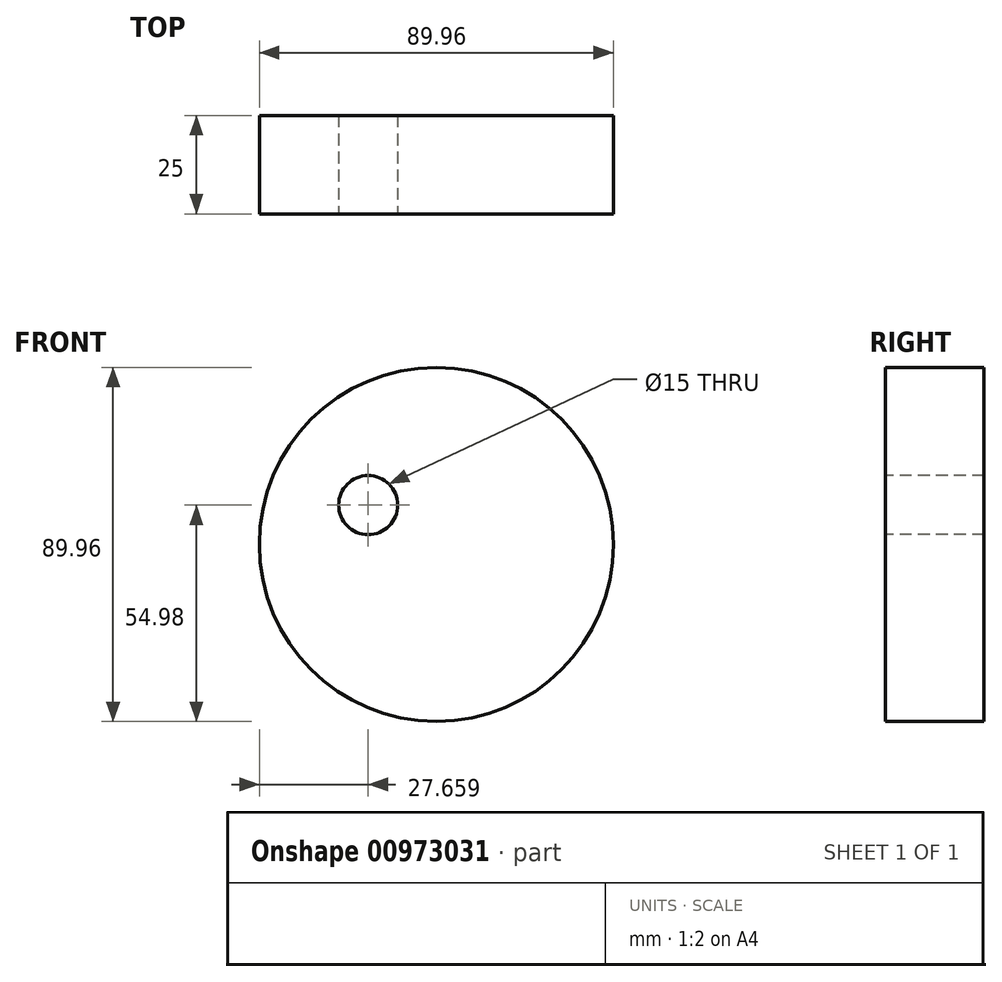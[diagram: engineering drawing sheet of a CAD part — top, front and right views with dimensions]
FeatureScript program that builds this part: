
annotation { "Feature Type Name" : "Feature", "Feature Type Description" : "" }
export const myFeature = defineFeature(function(context is Context, id is Id, definition is map)
    precondition{}
    {
        {
            var Q0;
            Q0=qCreatedBy(makeId("Front.planeOp"),FACE);
            var sketch = newSketch(context, id + "F0", { "sketchPlane" : qUnion([Q0])});
            skCircle(sketch, "E0", {"center": v(0, 0) * mm, "radius": 44.98 * mm});
            skSolve(sketch);
        }
        {
            var Q0;
            Q0=makeQuery(id+"F0.imprint","IMPRINT",FACE,{"disambiguationData":[TD([[makeQuery(id+"F0.imprint","IMPRINT",EDGE,{"derivedFrom":sQuery(id+"F0.wireOp",EDGE,"E0")}),1.0]])]});
            extrude(context, id + "F1", {"entities" : qUnion([Q0]), "depth" : 25 * mm, "offsetDistance" : 25 * mm});
        }
        {
            var Q0;
            Q0=makeQuery(id+"F1.opExtrude","CAP_FACE",FACE,{"disambiguationData":[OSD([sQuery(id+"F0.wireOp",EDGE,"E0")])],"isStart":false});
            var sketch = newSketch(context, id + "F2", { "sketchPlane" : qUnion([Q0])});
            skCircle(sketch, "E1", {"center": v(-17.32, 10) * mm, "radius": 7.5 * mm});
            skLineSegment(sketch, "E2", {"start": v(0, 0) * mm, "end": v(-17.32, 10) * mm, "construction": true});
            skSolve(sketch);
        }
        {
            var Q0;
            Q0 = qSketchRegion(id + "F2", true);
            extrude(context, id + "F3", {"entities" : qUnion([Q0]), "operationType" : NewBodyOperationType.REMOVE, "oppositeDirection" : true, "depth" : 25 * mm, "offsetDistance" : 25 * mm});
        }
    });
